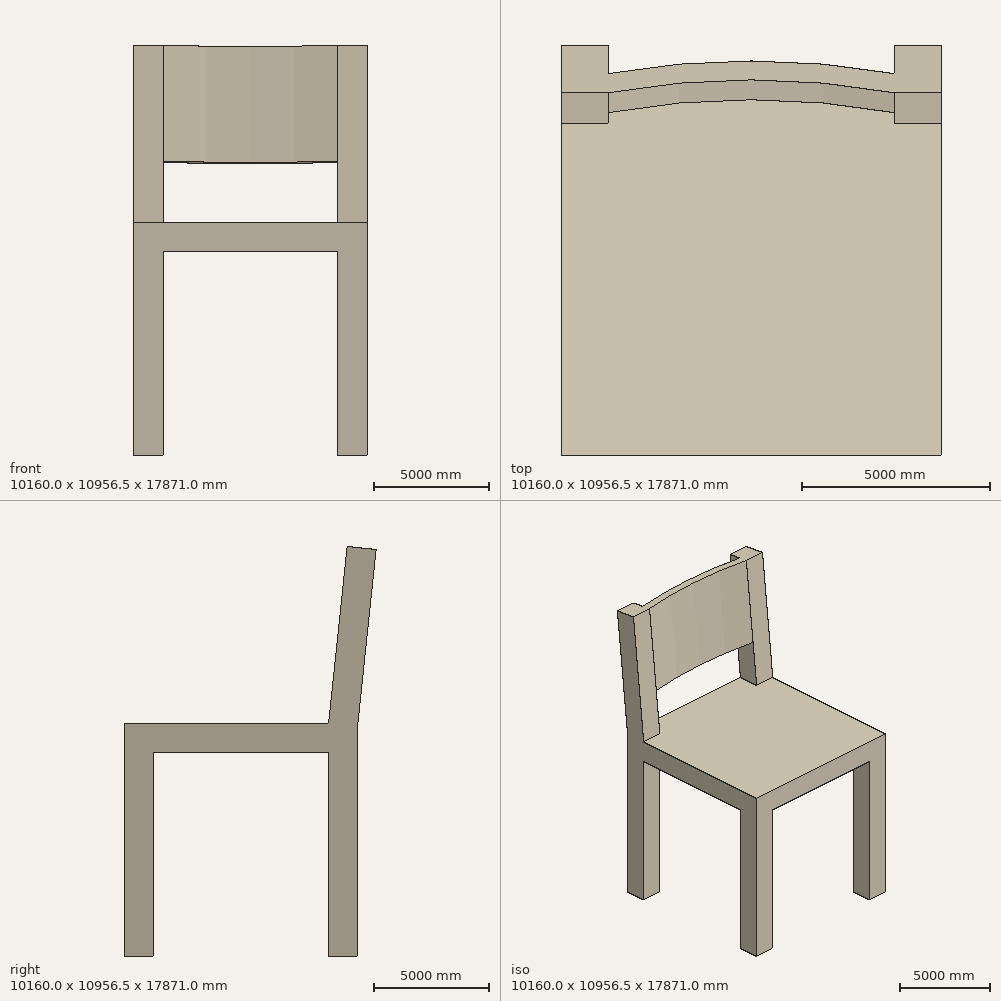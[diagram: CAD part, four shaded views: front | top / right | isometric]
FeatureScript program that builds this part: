
annotation { "Feature Type Name" : "Feature", "Feature Type Description" : "" }
export const myFeature = defineFeature(function(context is Context, id is Id, definition is map)
    precondition{}
    {
        {
            var Q0;
            Q0=qCreatedBy(makeId("Top.planeOp"),FACE);
            var sketch = newSketch(context, id + "F0", { "sketchPlane" : qUnion([Q0])});
            skLineSegment(sketch, "E0.bottom", {"start": v(-508, 9727.53) * mm, "end": v(9652, 9727.53) * mm});
            skLineSegment(sketch, "E0.top", {"start": v(-508, -432.47) * mm, "end": v(9652, -432.47) * mm});
            skLineSegment(sketch, "E0.left", {"start": v(-508, 9727.53) * mm, "end": v(-508, -432.47) * mm});
            skLineSegment(sketch, "E0.right", {"start": v(9652, 9727.53) * mm, "end": v(9652, -432.47) * mm});
            skSolve(sketch);
        }
        {
            var Q0;
            Q0=makeQuery(id+"F0.imprint","IMPRINT",FACE,{"disambiguationData":[TD([[makeQuery(id+"F0.imprint","IMPRINT",EDGE,{"derivedFrom":sQuery(id+"F0.wireOp",EDGE,"E0.bottom")}),-1.0]])]});
            extrude(context, id + "F1", {"entities" : qUnion([Q0]), "depth" : 10160 * mm, "offsetDistance" : 25.4 * mm});
        }
        {
            var Q0;
            Q0=makeQuery(id+"F1.opExtrude","SWEPT_FACE",FACE,{"disambiguationData":[OSD([sQuery(id+"F0.wireOp",EDGE,"E0.top")])]});
            var sketch = newSketch(context, id + "F2", { "sketchPlane" : qUnion([Q0])});
            skLineSegment(sketch, "E1", {"start": v(-508, 0) * mm, "end": v(762, 0) * mm});
            skLineSegment(sketch, "E2", {"start": v(762, 0) * mm, "end": v(762, 8890) * mm});
            skLineSegment(sketch, "E3", {"start": v(9652, 0) * mm, "end": v(8382, 0) * mm});
            skLineSegment(sketch, "E4", {"start": v(8382, 0) * mm, "end": v(8382, 8890) * mm});
            skLineSegment(sketch, "E5", {"start": v(762, 8890) * mm, "end": v(8382, 8890) * mm});
            skSolve(sketch);
        }
        {
            var Q0;
            {var subQ0=sQuery(id+"F2.wireOp",EDGE,"E2");Q0=makeQuery(id+"F2.imprint","IMPRINT",FACE,{"disambiguationData":[TD([[makeQuery(id+"F2.imprint","IMPRINT",EDGE,{"derivedFrom":subQ0}),-1.0]])]});}
            extrude(context, id + "F3", {"entities" : qUnion([Q0]), "operationType" : NewBodyOperationType.REMOVE, "endBound" : BoundingType.THROUGH_ALL, "oppositeDirection" : true, "depth" : 4368.8 * mm, "offsetDistance" : 25.4 * mm});
        }
        {
            var Q0;
            Q0=makeQuery(id+"F1.opExtrude","SWEPT_FACE",FACE,{"disambiguationData":[OSD([sQuery(id+"F0.wireOp",EDGE,"E0.right")])]});
            var sketch = newSketch(context, id + "F4", { "sketchPlane" : qUnion([Q0])});
            skLineSegment(sketch, "E6", {"start": v(-432.47, 0) * mm, "end": v(837.53, 0) * mm});
            skLineSegment(sketch, "E7", {"start": v(837.53, 0) * mm, "end": v(837.53, 8890) * mm});
            skLineSegment(sketch, "E8", {"start": v(9727.53, 0) * mm, "end": v(8457.53, 0) * mm});
            skLineSegment(sketch, "E9", {"start": v(8457.53, 0) * mm, "end": v(8457.53, 8890) * mm});
            skLineSegment(sketch, "E10", {"start": v(8457.53, 8890) * mm, "end": v(837.53, 8890) * mm});
            skSolve(sketch);
        }
        {
            var Q0;
            {var subQ0=sQuery(id+"F4.wireOp",EDGE,"E7");Q0=makeQuery(id+"F4.imprint","IMPRINT",FACE,{"disambiguationData":[TD([[makeQuery(id+"F4.imprint","IMPRINT",EDGE,{"derivedFrom":subQ0}),-1.0]])]});}
            extrude(context, id + "F5", {"entities" : qUnion([Q0]), "operationType" : NewBodyOperationType.REMOVE, "endBound" : BoundingType.THROUGH_ALL, "oppositeDirection" : true, "depth" : 25.4 * mm, "offsetDistance" : 25.4 * mm});
        }
        {
            var Q0;
            Q0=makeQuery(id+"F1.opExtrude","SWEPT_FACE",FACE,{"disambiguationData":[OSD([sQuery(id+"F0.wireOp",EDGE,"E0.bottom")])]});
            var Q1;
            Q1=makeQuery(id+"F1.opExtrude","CAP_VERTEX",VERTEX,{"disambiguationData":[OSD([sQuery(id+"F0.wireOp",EDGE,"E0.bottom"),sQuery(id+"F0.wireOp",EDGE,"E0.right")])],"isStart":false});
            cPlane(context, id + "F6", {"entities" : qUnion([Q0, Q1]), "cplaneType" : CPlaneType.PLANE_POINT, "offset" : 25.4 * mm, "width" : 152.4 * mm, "height" : 152.4 * mm});
        }
        {
            var Q0;
            Q0=qCreatedBy(id+"F6.planeOp",FACE);
            var Q1;
            Q1=makeQuery(id+"F1.opExtrude","CAP_EDGE",EDGE,{"disambiguationData":[OSD([sQuery(id+"F0.wireOp",EDGE,"E0.bottom")])],"isStart":false});
            cPlane(context, id + "F7", {"entities" : qUnion([Q0, Q1]), "cplaneType" : CPlaneType.LINE_ANGLE, "offset" : 25.4 * mm, "angle" : 6 * degree, "oppositeDirection" : true, "width" : 152.4 * mm, "height" : 152.4 * mm});
        }
        {
            var Q0;
            Q0=qCreatedBy(id+"F7.planeOp",FACE);
            var sketch = newSketch(context, id + "F8", { "sketchPlane" : qUnion([Q0])});
            skLineSegment(sketch, "E11.bottom", {"start": v(-508, 18741.15) * mm, "end": v(9652, 18741.15) * mm});
            skLineSegment(sketch, "E11.top", {"start": v(-508, 11121.15) * mm, "end": v(9652, 11121.15) * mm});
            skLineSegment(sketch, "E11.left", {"start": v(-508, 18741.15) * mm, "end": v(-508, 11121.15) * mm});
            skLineSegment(sketch, "E11.right", {"start": v(9652, 18741.15) * mm, "end": v(9652, 11121.15) * mm});
            skSolve(sketch);
        }
        {
            var Q0;
            Q0=makeQuery(id+"F8.imprint","IMPRINT",FACE,{"disambiguationData":[TD([[makeQuery(id+"F8.imprint","IMPRINT",EDGE,{"derivedFrom":sQuery(id+"F8.wireOp",EDGE,"E11.bottom")}),-1.0]])]});
            extrude(context, id + "F9", {"entities" : qUnion([Q0]), "depth" : 1270 * mm, "offsetDistance" : 25.4 * mm});
        }
        {
            var Q0;
            Q0=makeQuery(id+"F9.opExtrude","CAP_FACE",FACE,{"disambiguationData":[OSD([sQuery(id+"F8.wireOp",EDGE,"E11.bottom"),sQuery(id+"F8.wireOp",EDGE,"E11.top"),sQuery(id+"F8.wireOp",EDGE,"E11.left"),sQuery(id+"F8.wireOp",EDGE,"E11.right")])],"isStart":false});
            var sketch = newSketch(context, id + "F10", { "sketchPlane" : qUnion([Q0])});
            skLineSegment(sketch, "E12.bottom", {"start": v(762, 18741.15) * mm, "end": v(8382, 18741.15) * mm});
            skLineSegment(sketch, "E12.top", {"start": v(762, 11121.15) * mm, "end": v(8382, 11121.15) * mm});
            skLineSegment(sketch, "E12.left", {"start": v(762, 18741.15) * mm, "end": v(762, 11121.15) * mm});
            skLineSegment(sketch, "E12.right", {"start": v(8382, 18741.15) * mm, "end": v(8382, 11121.15) * mm});
            skLineSegment(sketch, "E13", {"start": v(9652, 11121.15) * mm, "end": v(8382, 11121.15) * mm});
            skSolve(sketch);
        }
        {
            var Q0;
            Q0=makeQuery(id+"F10.imprint","IMPRINT",FACE,{"disambiguationData":[TD([[makeQuery(id+"F10.imprint","IMPRINT",EDGE,{"derivedFrom":sQuery(id+"F10.wireOp",EDGE,"E12.bottom")}),-1.0]])]});
            extrude(context, id + "F11", {"entities" : qUnion([Q0]), "operationType" : NewBodyOperationType.REMOVE, "endBound" : BoundingType.THROUGH_ALL, "oppositeDirection" : true, "depth" : 25.4 * mm, "offsetDistance" : 25.4 * mm});
        }
        {
            var Q0;
            {var subQ1=sQuery(id+"F8.wireOp",EDGE,"E11.left");var subQ2=sQuery(id+"F8.wireOp",EDGE,"E11.top");Q0=makeQuery(id+"F11.boolean.opBoolean","SPLIT",FACE,{"disambiguationData":[TD([makeQuery(id+"F9.opExtrude","SWEPT_FACE",FACE,{"disambiguationData":[OSD([subQ1])]})])],"derivedFrom":makeQuery(id+"F9.opExtrude","SWEPT_FACE",FACE,{"disambiguationData":[OSD([subQ2])]})});}
            extrude(context, id + "F12", {"entities" : qUnion([Q0]), "operationType" : NewBodyOperationType.ADD, "endBound" : BoundingType.UP_TO_NEXT, "depth" : 25.4 * mm, "offsetDistance" : 25.4 * mm});
        }
        {
            var Q0;
            {var subQ0=sQuery(id+"F8.wireOp",EDGE,"E11.right");var subQ2=sQuery(id+"F8.wireOp",EDGE,"E11.top");Q0=makeQuery(id+"F11.boolean.opBoolean","SPLIT",FACE,{"disambiguationData":[TD([makeQuery(id+"F9.opExtrude","SWEPT_FACE",FACE,{"disambiguationData":[OSD([subQ0])]})])],"derivedFrom":makeQuery(id+"F9.opExtrude","SWEPT_FACE",FACE,{"disambiguationData":[OSD([subQ2])]})});}
            extrude(context, id + "F13", {"entities" : qUnion([Q0]), "operationType" : NewBodyOperationType.ADD, "endBound" : BoundingType.UP_TO_NEXT, "depth" : 25.4 * mm, "offsetDistance" : 25.4 * mm});
        }
        {
            var Q0;
            {var subQ1=sQuery(id+"F8.wireOp",EDGE,"E11.left");var subQ3=sQuery(id+"F8.wireOp",EDGE,"E11.bottom");Q0=makeQuery(id+"F11.boolean.opBoolean","SPLIT",FACE,{"disambiguationData":[TD([makeQuery(id+"F9.opExtrude","SWEPT_FACE",FACE,{"disambiguationData":[OSD([subQ1])]})])],"derivedFrom":makeQuery(id+"F9.opExtrude","SWEPT_FACE",FACE,{"disambiguationData":[OSD([subQ3])]})});}
            var sketch = newSketch(context, id + "F14", { "sketchPlane" : qUnion([Q0])});
            skArc(sketch, "E14", {"start": v(8382.81, 7342.23) * mm, "mid": v(4572.4, 7688.29) * mm, "end": v(762, 7342.23) * mm});
            skArc(sketch, "E15.0", {"start": v(8474.33, 7841.92) * mm, "mid": v(4572.4, 8196.29) * mm, "end": v(670.48, 7841.92) * mm});
            skLineSegment(sketch, "E16", {"start": v(8382.81, 7342.23) * mm, "end": v(8474.33, 7841.92) * mm});
            skLineSegment(sketch, "E17", {"start": v(762, 7342.23) * mm, "end": v(670.48, 7841.92) * mm});
            skSolve(sketch);
        }
        {
            var Q0;
            {var subQ0=sQuery(id+"F14.wireOp",EDGE,"E14");Q0=makeQuery(id+"F14.imprint","IMPRINT",FACE,{"disambiguationData":[TD([[makeQuery(id+"F14.imprint","IMPRINT",EDGE,{"derivedFrom":subQ0}),-1.0]])]});}
            extrude(context, id + "F15", {"entities" : qUnion([Q0]), "operationType" : NewBodyOperationType.ADD, "oppositeDirection" : true, "depth" : 5080 * mm, "offsetDistance" : 25.4 * mm});
        }
    });
